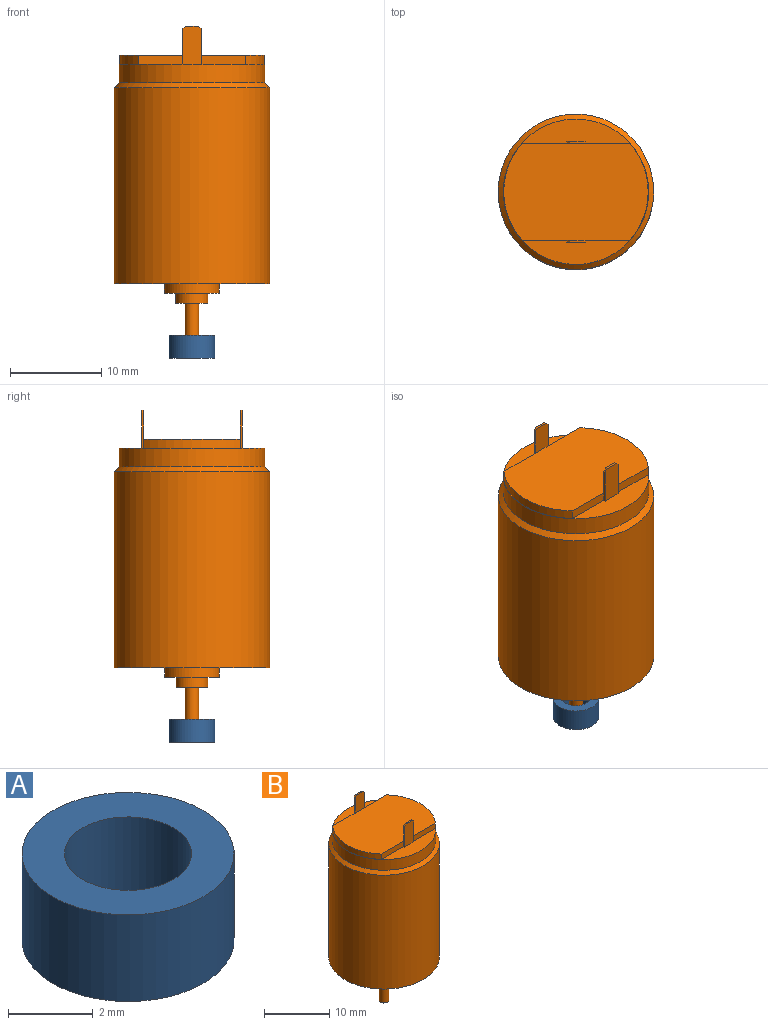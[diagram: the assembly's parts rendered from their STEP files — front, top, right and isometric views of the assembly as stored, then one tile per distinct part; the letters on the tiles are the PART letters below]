
ASSEMBLY  parts=2 mates=1
PART A: 4 faces, bbox 5x5x2.5 mm
  f0: cylinder r=1.5mm len=3mm, axis (0,0,-1), area 23.6mm2, adj f2,f3
  f1: cylinder r=2.5mm len=5mm, axis (0,0,-1), area 39.3mm2, adj f2,f3
  f2: plane 5x5mm, normal (0,0,1), area 12.6mm2, adj f0,f1
  f3: plane 5x5mm, normal (0,0,-1), area 12.6mm2, adj f0,f1
PART B: 44 faces, bbox 17x17x36.3 mm
  f0: plane 4.86x1mm, normal (0,1,0), area 4.9mm2, adj f1,f26,f29,f36
  f1: plane 15.9x15.9mm, normal (0,0,1), area 43.9mm2, adj f0,f2,f6,f25,f26,f27,f28,f31
  f2: plane 4.86x1mm, normal (0,-1,0), area 4.9mm2, adj f1,f26,f29,f31
  f3: cylinder r=8.5mm len=21.45mm, axis (0,0,-1), area 1145.6mm2, adj f4,f5
  f4: plane 17x17mm, normal (0,0,-1), area 186.6mm2, adj f3,f7,f13,f15,f17,f19,f21,f23
  f5: cone r=7.95mm half-angle=45deg, axis (0,0,-1), area 40.2mm2, adj f3,f6
  f6: cylinder r=7.95mm len=15.9mm, axis (0,0,-1), area 99.9mm2, adj f1,f5
  f7: cylinder r=3mm len=6mm, axis (0,0,1), area 18.8mm2, adj f4,f8
  f8: plane 6x6mm, normal (0,0,-1), area 18.7mm2, adj f7,f9
  f9: cylinder r=1.75mm len=3.5mm, axis (0,0,1), area 12.1mm2, adj f8,f10
  f10: plane 3.5x3.5mm, normal (0,0,-1), area 7.9mm2, adj f9,f11
  f11: cylinder r=0.75mm len=6mm, axis (0,0,1), area 28.3mm2, adj f10,f12
  f12: plane 1.5x1.5mm, normal (0,0,-1), area 1.8mm2, adj f11
  f13: cylinder r=0.8mm len=1.6mm, axis (0,0,-1), area 8mm2, adj f4,f14
  f14: plane 1.6x1.6mm, normal (0,0,-1), area 2mm2, adj f13
  f15: cylinder r=0.8mm len=1.6mm, axis (0,0,-1), area 8mm2, adj f4,f16
  f16: plane 1.6x1.6mm, normal (0,0,-1), area 2mm2, adj f15
  f17: cylinder r=0.8mm len=1.6mm, axis (0,0,-1), area 8mm2, adj f4,f18
  f18: plane 1.6x1.6mm, normal (0,0,-1), area 2mm2, adj f17
  f19: cylinder r=0.8mm len=1.6mm, axis (0,0,-1), area 8mm2, adj f4,f20
  f20: plane 1.6x1.6mm, normal (0,0,-1), area 2mm2, adj f19
  f21: cylinder r=0.8mm len=1.6mm, axis (0,0,-1), area 8mm2, adj f4,f22
  f22: plane 1.6x1.6mm, normal (0,0,-1), area 2mm2, adj f21
  f23: cylinder r=0.8mm len=1.6mm, axis (0,0,-1), area 8mm2, adj f4,f24
  f24: plane 1.6x1.6mm, normal (0,0,-1), area 2mm2, adj f23
  f25: plane 4.86x1mm, normal (0,-1,0), area 4.9mm2, adj f1,f28,f29,f32
  f26: cylinder r=7.9mm len=10.6mm, axis (0,0,-1), area 11.6mm2, adj f0,f1,f2,f29
  f27: plane 4.86x1mm, normal (0,1,0), area 4.9mm2, adj f1,f28,f29,f38
  f28: cylinder r=7.9mm len=10.6mm, axis (0,0,-1), area 11.6mm2, adj f1,f25,f27,f29
  f29: plane 15.8x10.6mm, normal (0,0,1), area 153.9mm2, adj f0,f2,f25,f26,f27,f28,f30,f35
  f30: plane 3.2x2mm, normal (0,1,0), area 6.3mm2, adj f29,f31,f32,f34,f42,f43
  f31: plane 3.9x0.2mm, normal (1,0,0), area 0.8mm2, adj f1,f2,f30,f33,f43
  f32: plane 3.9x0.2mm, normal (-1,0,0), area 0.8mm2, adj f1,f25,f30,f33,f42
  f33: plane 4.2x2mm, normal (0,-1,0), area 8.3mm2, adj f1,f31,f32,f34,f42,f43
  f34: plane 1.4x0.2mm, normal (0,0,1), area 0.3mm2, adj f30,f33,f42,f43
  f35: plane 3.2x2mm, normal (0,-1,0), area 6.3mm2, adj f29,f36,f38,f39,f40,f41
  f36: plane 3.9x0.2mm, normal (1,0,0), area 0.8mm2, adj f0,f1,f35,f37,f41
  f37: plane 4.2x2mm, normal (0,1,0), area 8.3mm2, adj f1,f36,f38,f39,f40,f41
  f38: plane 3.9x0.2mm, normal (-1,0,0), area 0.8mm2, adj f1,f27,f35,f37,f40
  f39: plane 1.4x0.2mm, normal (0,0,1), area 0.3mm2, adj f35,f37,f40,f41
  f40: plane 0.3x0.3mm, normal (-0.71,0,0.71), area 0.1mm2, adj f35,f37,f38,f39
  f41: plane 0.3x0.3mm, normal (0.71,0,0.71), area 0.1mm2, adj f35,f36,f37,f39
  f42: plane 0.3x0.3mm, normal (-0.71,0,0.71), area 0.1mm2, adj f30,f32,f33,f34
  f43: plane 0.3x0.3mm, normal (0.71,0,0.71), area 0.1mm2, adj f30,f31,f33,f34
PLACE A at identity
PLACE B t=(0,0,8.1)mm
MATE revolute B.f11 <-> A.f1  axis (0,0,-1) through (0,0,0)mm
